# Revit family: IS_iLifeS_T4738_BIM_NL
name_source: partatom
category: Plumbing Fixtures
units: mm (PartAtom-declared; Revit-internal decimal feet)

## family parameters
Always vertical = No
Cut with Voids When Loaded = No
OmniClass Number = 23.45.05.21.11.11
OmniClass Title = Water Operated Water Closets
Part Type = Normal
Room Calculation Point = No
Round Connector Dimension = Use Diameter
Shared = No
Work Plane-Based = No

## types (1)
- T473801 - i.life S Wall Hung 48 cm Rim less WC Bowl - White
    Accessories = https://www.idealstandard.nl
    Afmetingen = 480 x 338 x 353 mm
    AfstandsEenheid = Millimeter
    Afwerking = Weiß
    AreaUnits = millimetres
    Artikelnummer = T473801
    Artikelomschrijving = Ideal Standard i.life S, wandhängendes Becken, RimLS+, verdeckte Befestigung, Easyfix+, kompakt 48 cm,
inkl. dedizierter Sitzbezug, Softclose, weiß, Bildkarton, EU-Palette
    AssetType = Fixed
    Auteur = Ideal Standard
    BIMObjectName = IS_IdealStandard_WC pans_i.lifeS_T4738
    BIMobject category = Toilets
    BIMobject category code = toilets
    BIMobject main category = Sanitary
    BIMobject main category code = sanitary
    BarCode = 8014140496052
    Beschrijvinggarantie = Herstellergarantie
    BimObjectNaam = IS_IdealStandard_WC pans_i.lifeS_T4738
    Brand = Ideal Standard
    Brand url = https://www.idealstandard.nl
    Breedte = 353.426368
    BrutoGewicht = 0
    Category = Sanitary
    Color = Weiß
    ConnectionType = Plumbing
    Cost = 0 $
    CurrencyUnit = €
    CurrentRevision = 1
    Date of publishing = 27/05/2022
    Description = Ideal Standard i.life S, wallhung bowl, RimLS+, hidden fixation, Easyfix+, compact 48 cm,  
incl. dedicated seat wrapover, softclose, white, picture box, EU pallet
    Diepte = 480 mm  [stored 1.5748 ft]
    DurationUnit = Years
    DuurEenheid = Jahre
    Edition number = 1
    Eigenschappen = Ideal Standard i.life S, wandhängendes Becken, RimLS+, verdeckte Befestigung, Easyfix+, kompakt 48 cm,
inkl. dedizierter Sitzbezug, Softclose, weiß, Bildkarton, EU-Palette
    ElementType = Fixed
    ExpectedLife = 99
    Features = Ideal Standard i.life S, wallhung bowl, RimLS+, hidden fixation, Easyfix+, compact 48 cm,  
incl. dedicated seat wrapover, softclose, white, picture box, EU pallet
    Finish = White
    GTIN code = https://8014140496052
    Garantieunits = Jahre
    Help = https://www.idealstandard.nl
    Hoogte = 337.930778790414
    Hulp = https://www.idealstandard.nl
    IFC Classification = Sanitary Terminal
    IfcExportAs = IfcSanitaryTerminalType
    IfcExportType = TOILETPAN
    Installatieinstructies = https://www.idealstandard.nl
    Installation instructions = https://www.idealstandard.nl
    InstallationInstructions = https://www.idealstandard.nl
    Kleur = Weiß
    Lengte = 480 mm  [stored 1.5748 ft]
    LinearUnits = Millimetres
    MainColor = White
    MaintenanceInformation = https://www.idealstandard.nl
    Manufacturer = Ideal Standard
    Manufacturer name = Ideal Standard
    ManufacturerURL = https://www.idealstandard.nl
    Materiaal = Glasiges China
    MateriaalWC = Glasiges China
    Material = Vitrous China
    Material main = Vitrous China
    Merk = Ideal Standard
    Model = T473801
    ModelNumber = T473801
    ModelReference = i.life S Wall Hung 48 cm Rim less WC Bowl
    NBS Reference Code = 45-35-70/384
    NBS Reference Description = WC pans
    Name = WC pans_i.lifeS_T4738_IdealStandard
    NettWeight = 21.14
    Nettogewicht = 21.14
    NominalDepth = 480 mm  [stored 1.5748 ft]
    NominalHeight = 338 mm
    NominalLength = 480 mm  [stored 1.5748 ft]
    NominalWidth = 353 mm
    Normen = WC pans_i.lifeS_T4738_IdealStandard
    OmniClass Code = 23-31 19 00
    OmniClass Description = Toilets
    OppervlakteEenheid = Millimeter
    PanColor = White
    PanMaterial = Glasporzellan
    PanMounting = wandhängende WC-Pfanne
    PredefinedType = Sanitary
    Product Guid = db5d8a3f-3e1b-40b5-8cb5-638a98d1101e
    Product SKU = T4738
    Product certification = https://www.idealstandard.nl
    Product data url = https://bimobject.com
    Product family = I.life S
    Product group = Sanitry: WC Pans
    Product name = i.life S Wall Hung 48 cm Rim less WC Bowl
    Product url = https://www.idealstandard.nl
    ProductInformation = https://www.idealstandard.nl
    Productinformatie = https://www.idealstandard.nl
    QR code = http://bimobject.com
    Referentie = i.life S Wall Hung 48 cm Rim less WC Bowl
    ReplacementCost = 0
    Revisie = 1
    Shape = Sculpture
    Size = 480 x 338 x 353 mm
    Space = Internal
    SpareParts = https://www.idealstandard.nl
    Technical description = https://www.idealstandard.nl
    Telefoonnummer = 077 355 08 08
    ToiletPanType = Wall Hung WC Pan
    ToiletType = Wall Hung WC Pan
    Typeconnectie = Installation
    UNSPSC Code = 301815
    URL = https://www.idealstandard.nl
    Uniclass 2015 Code = Pr_40_20_93_94
    Uniclass 2015 Name = WC pans
    Uniclass2015Beschrijving = WC pans
    Uniclass2015Code = Pr_40_20_93_94
    Uniclass2015Referentie = Pr_40_20_93_94
    Uniclass2015Title = WC pans
    Uniclass2015Version = v.25
    Urlproducent = https://www.idealstandard.nl
    ValutaEenheid = Euro
    Versie = 1
    Version = 1
    Vervangingskosten = 0
    VolumeUnits = Litres
    Volumeunits = Liter
    Vorm = geformt
    WRASURL = https://www.wrasapprovals.co.uk
    WarrantyDescription = manufacturer warranty
    WarrantyDurationUnit = years
    Wisselstukken = https://www.idealstandard.nl
    Youtube clip = https://www.youtube.com

note: [stored X ft] marks values corroborated as IEEE doubles in the binary element streams (Revit-internal decimal feet)

## geometry (parser evidence)
native form markers: Sweep x2
no freeform markers — native parametric forms only
